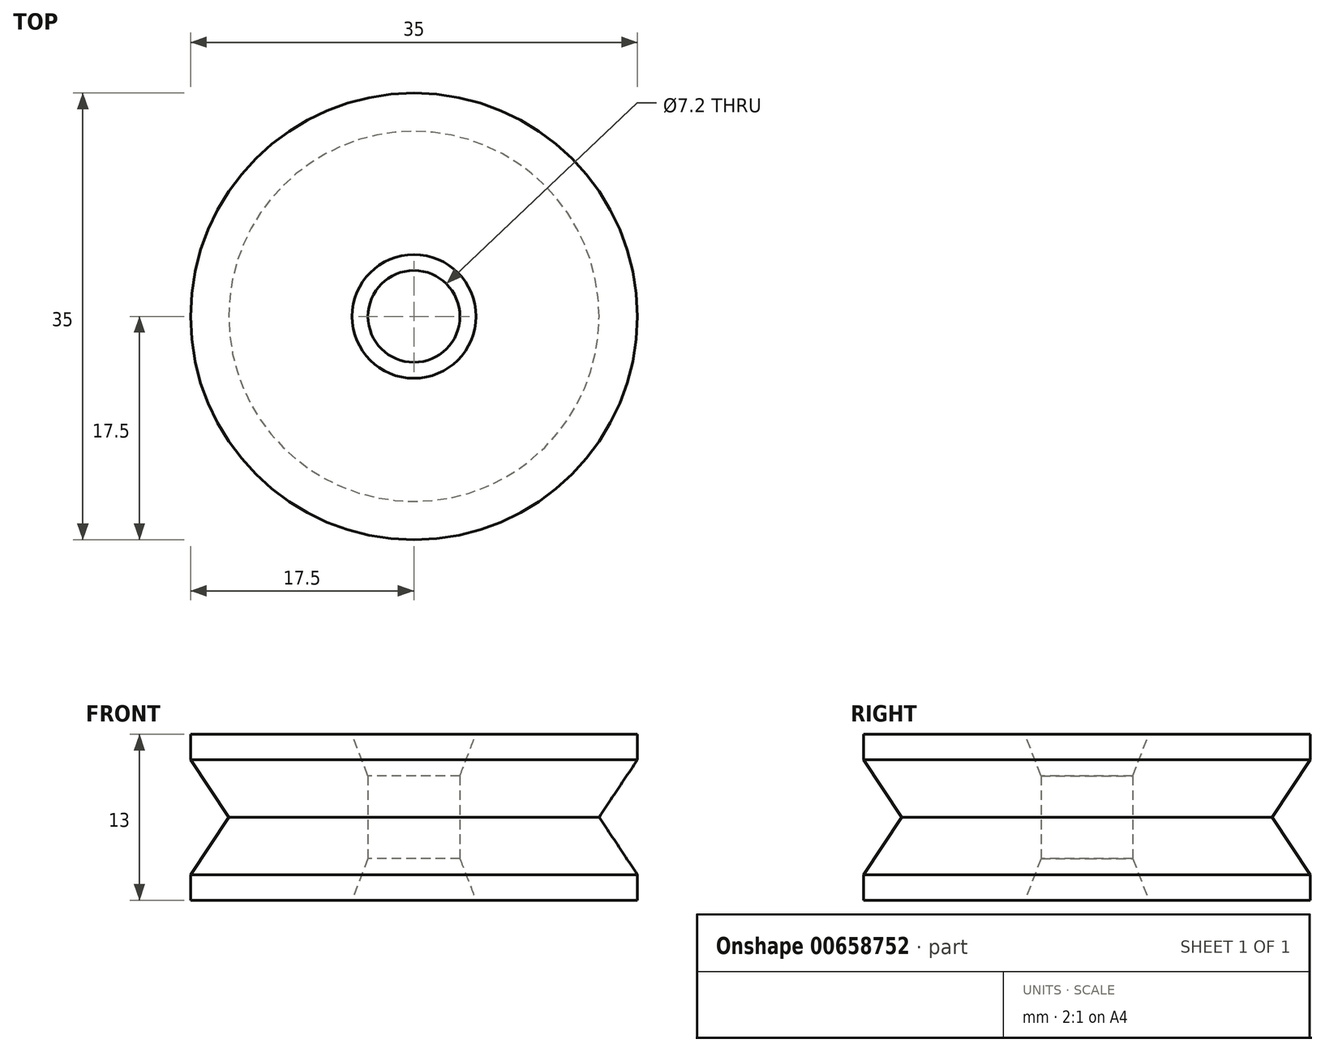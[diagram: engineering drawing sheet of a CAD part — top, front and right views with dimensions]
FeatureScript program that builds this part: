
annotation { "Feature Type Name" : "Feature", "Feature Type Description" : "" }
export const myFeature = defineFeature(function(context is Context, id is Id, definition is map)
    precondition{}
    {
        {
            var Q0;
            Q0=qCreatedBy(makeId("Top.planeOp"),FACE);
            var sketch = newSketch(context, id + "F0", { "sketchPlane" : qUnion([Q0])});
            skCircle(sketch, "E0", {"center": v(0, 0) * mm, "radius": 17.5 * mm});
            skCircle(sketch, "E1", {"center": v(0, 0) * mm, "radius": 3.6 * mm});
            skSolve(sketch);
        }
        {
            var Q0;
            Q0=makeQuery(id+"F0.imprint","IMPRINT",FACE,{"disambiguationData":[TD([[makeQuery(id+"F0.imprint","IMPRINT",EDGE,{"derivedFrom":sQuery(id+"F0.wireOp",EDGE,"E0")}),1.0]])]});
            extrude(context, id + "F1", {"entities" : qUnion([Q0]), "depth" : 13 * mm, "offsetDistance" : 25 * mm});
        }
        {
            var Q0;
            Q0=qCreatedBy(makeId("Front.planeOp"),FACE);
            var sketch = newSketch(context, id + "F2", { "sketchPlane" : qUnion([Q0])});
            skLineSegment(sketch, "E2", {"start": v(-17.5, 0) * mm, "end": v(-17.5, 15) * mm});
            skLineSegment(sketch, "E3", {"start": v(17.5, 13.02) * mm, "end": v(17.5, 0) * mm});
            skLineSegment(sketch, "E4", {"start": v(-17.5, 0) * mm, "end": v(-17.5, 12) * mm});
            skPoint(sketch, "E5", {"position": v(17.5, 11) * mm});
            skPoint(sketch, "E6", {"position": v(17.5, 2) * mm});
            skPoint(sketch, "E7", {"position": v(14.5, 6.51) * mm});
            skPoint(sketch, "E8", {"position": v(17.5, 6.51) * mm});
            skLineSegment(sketch, "E9", {"start": v(17.5, 11) * mm, "end": v(14.5, 6.51) * mm});
            skLineSegment(sketch, "E10", {"start": v(17.5, 2) * mm, "end": v(14.5, 6.51) * mm});
            skLineSegment(sketch, "E11", {"start": v(17.5, 11) * mm, "end": v(17.5, 2) * mm});
            skLineSegment(sketch, "E12", {"start": v(17.5, 13) * mm, "end": v(17.5, 0) * mm});
            skSolve(sketch);
        }
        {
            var Q0;
            Q0=makeQuery(id+"F2.imprint","IMPRINT",FACE,{"disambiguationData":[TD([[makeQuery(id+"F2.imprint","IMPRINT",EDGE,{"derivedFrom":sQuery(id+"F2.wireOp",EDGE,"E9")}),1.0]])]});
            var Q1;
            Q1=sQuery(id+"F0.wireOp",EDGE,"E0");
            revolve(context, id + "F3", {"operationType" : NewBodyOperationType.REMOVE, "entities" : qUnion([Q0]), "axis" : qUnion([Q1]), "revolveType" : RevolveType.FULL, "oppositeDirection" : true});
        }
        {
            var Q0;
            Q0=makeQuery(id+"F1.opExtrude","CAP_EDGE",EDGE,{"disambiguationData":[OSD([sQuery(id+"F0.wireOp",EDGE,"E1")])],"isStart":false});
            var Q1;
            Q1=makeQuery(id+"F1.opExtrude","CAP_EDGE",EDGE,{"disambiguationData":[OSD([sQuery(id+"F0.wireOp",EDGE,"E1")])],"isStart":true});
            chamfer(context, id + "F4", {"entities" : qUnion([Q0, Q1]), "chamferType" : ChamferType.TWO_OFFSETS, "width1" : 3.25 * mm, "oppositeDirection" : false, "width2" : 1.25 * mm, "tangentPropagation" : true});
        }
    });
